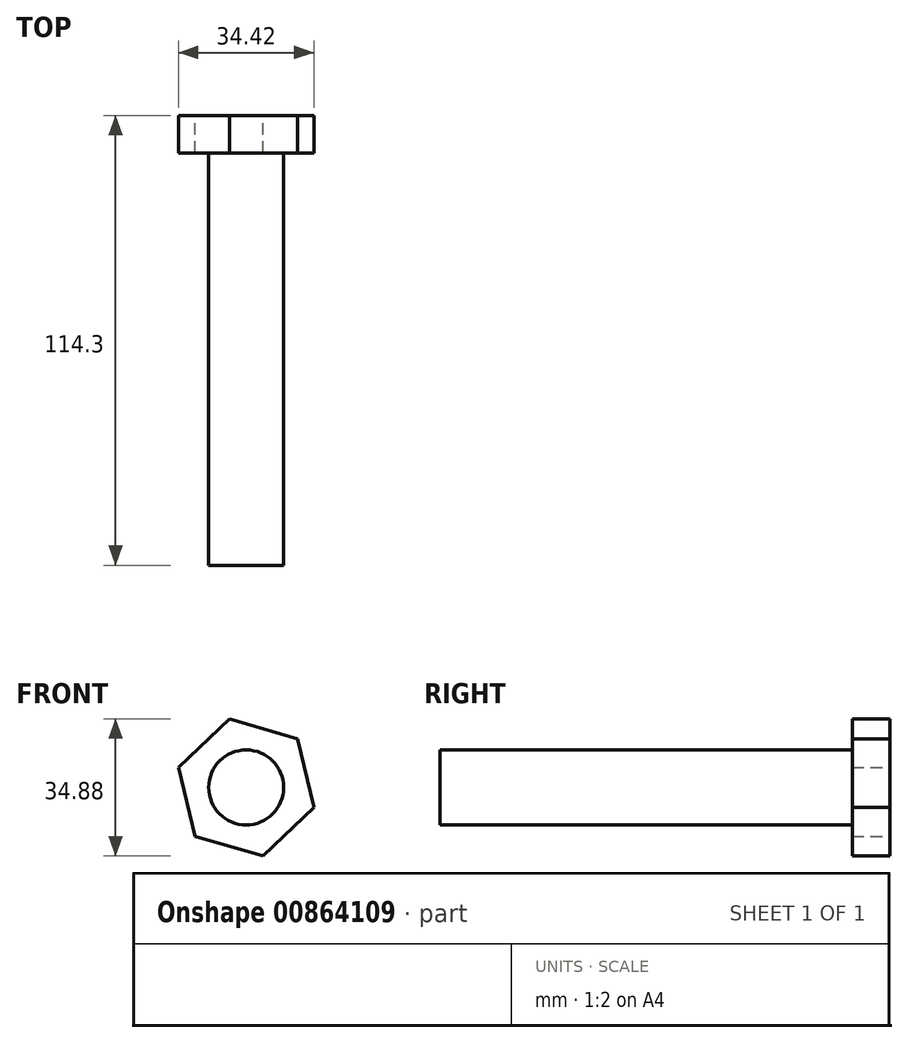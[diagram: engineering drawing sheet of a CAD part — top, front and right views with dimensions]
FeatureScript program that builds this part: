
annotation { "Feature Type Name" : "Feature", "Feature Type Description" : "" }
export const myFeature = defineFeature(function(context is Context, id is Id, definition is map)
    precondition{}
    {
        {
            var Q0;
            Q0=qCreatedBy(makeId("Front.planeOp"),FACE);
            var sketch = newSketch(context, id + "F0", { "sketchPlane" : qUnion([Q0])});
            skCircle(sketch, "E0", {"center": v(0, 0) * mm, "radius": 9.53 * mm});
            skCircle(sketch, "E1.cCircle", {"center": v(0, 0) * mm, "radius": 15.54 * mm, "construction": true});
            skLineSegment(sketch, "E1.0", {"start": v(-17.21, 5.06) * mm, "end": v(-4.22, 17.44) * mm});
            skLineSegment(sketch, "E1.1", {"start": v(-4.22, 17.44) * mm, "end": v(13, 12.37) * mm});
            skLineSegment(sketch, "E1.2", {"start": v(13, 12.37) * mm, "end": v(17.21, -5.06) * mm});
            skLineSegment(sketch, "E1.3", {"start": v(17.21, -5.06) * mm, "end": v(4.22, -17.44) * mm});
            skLineSegment(sketch, "E1.4", {"start": v(4.22, -17.44) * mm, "end": v(-13, -12.37) * mm});
            skLineSegment(sketch, "E1.5", {"start": v(-13, -12.37) * mm, "end": v(-17.21, 5.06) * mm});
            skPoint(sketch, "E1.0.midPoint", {"position": v(-10.72, 11.25) * mm});
            skSolve(sketch);
        }
        {
            var Q0;
            Q0=makeQuery(id+"F0.imprint","IMPRINT",FACE,{"disambiguationData":[TD([[makeQuery(id+"F0.imprint","IMPRINT",EDGE,{"derivedFrom":sQuery(id+"F0.wireOp",EDGE,"E0")}),-1.0]])]});
            var Q1;
            Q1=makeQuery(id+"F0.imprint","IMPRINT",FACE,{"disambiguationData":[TD([[makeQuery(id+"F0.imprint","IMPRINT",EDGE,{"derivedFrom":sQuery(id+"F0.wireOp",EDGE,"E0")}),1.0]])]});
            extrude(context, id + "F1", {"entities" : qUnion([Q0, Q1]), "depth" : 9.52 * mm, "offsetDistance" : 25.4 * mm});
        }
        {
            var Q0;
            Q0=makeQuery(id+"F0.imprint","IMPRINT",FACE,{"disambiguationData":[TD([[makeQuery(id+"F0.imprint","IMPRINT",EDGE,{"derivedFrom":sQuery(id+"F0.wireOp",EDGE,"E0")}),1.0]])]});
            extrude(context, id + "F2", {"entities" : qUnion([Q0]), "operationType" : NewBodyOperationType.ADD, "depth" : 88.9 * mm, "offsetDistance" : 25.4 * mm});
        }
        {
            var Q0;
            Q0=makeQuery(id+"F2.opExtrude","CAP_FACE",FACE,{"disambiguationData":[OSD([sQuery(id+"F0.wireOp",EDGE,"E0")])],"isStart":false});
            extrude(context, id + "F3", {"entities" : qUnion([Q0]), "operationType" : NewBodyOperationType.ADD, "depth" : 25.4 * mm, "offsetDistance" : 25.4 * mm});
        }
    });
